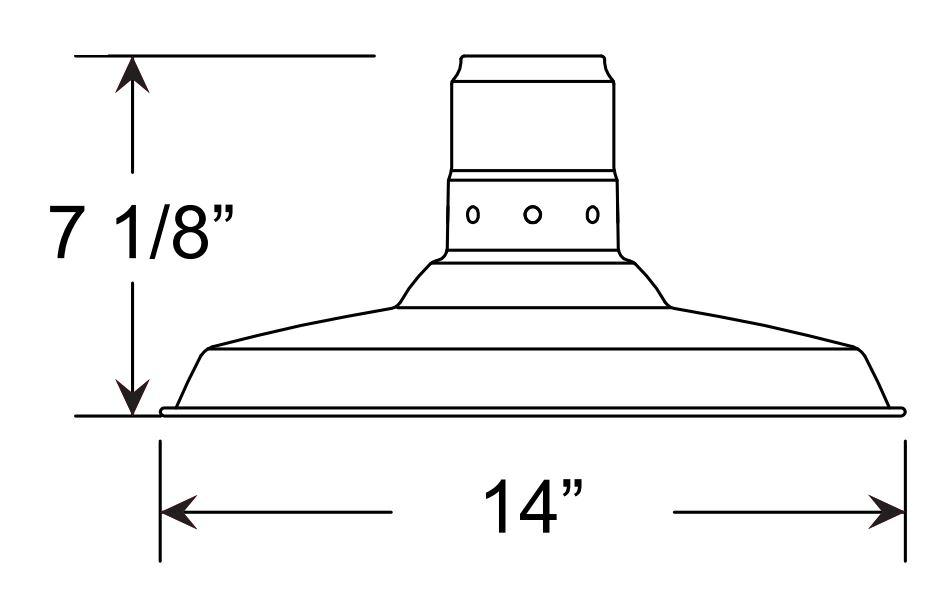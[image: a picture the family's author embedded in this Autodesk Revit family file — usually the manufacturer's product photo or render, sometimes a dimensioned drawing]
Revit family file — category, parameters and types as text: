
# Revit family: SPO-BP MB
name_source: partatom
category: Lighting Fixtures
units: mm (PartAtom-declared; Revit-internal decimal feet)

## family parameters
Always vertical = Yes
Cut with Voids When Loaded = No
Light Source = Yes
OmniClass Number = 23.80.70.00
OmniClass Title = Lighting
Part Type = Normal
Room Calculation Point = No
Round Connector Dimension = Use Diameter
Shared = No
Work Plane-Based = No

## types (1)
- SPO-BP
    Apparent Load = 60 VA
    Body Colour = Spun aluminium
    Body Material = body
    Color Filter = 16777215
    Construction Material = Heavy Duty spun aluminum.
    Default Elevation = 0' - 0"
    Description = 120-277 Voltage
    Dimming Lamp Color Temperature Shift = <None>
    Fixture Diameter = 0' - 1 1/2"
    Fixture Height = 0' - 2 1/2"
    GLASS = Glass
    Lamp = MED-BASE
    Load Classification = Lighting
    Manufacturer = ANP Lighting
    Model = SPO-BP
    Photometric Web File = generic.ies
    Power Factor = 1
    Ring = RING
    SPO-BP = Yes
    Tilt Angle = 90.00°
    URL = https://www.anplighting.com
    Voltage = 277 V
    Warranty = 5 year limited warranty
    Wattage Comments = 60W Max
    Weight = 0.30 lbs

## geometry (parser evidence)
native form markers: Sweep x23
no freeform markers — native parametric forms only
